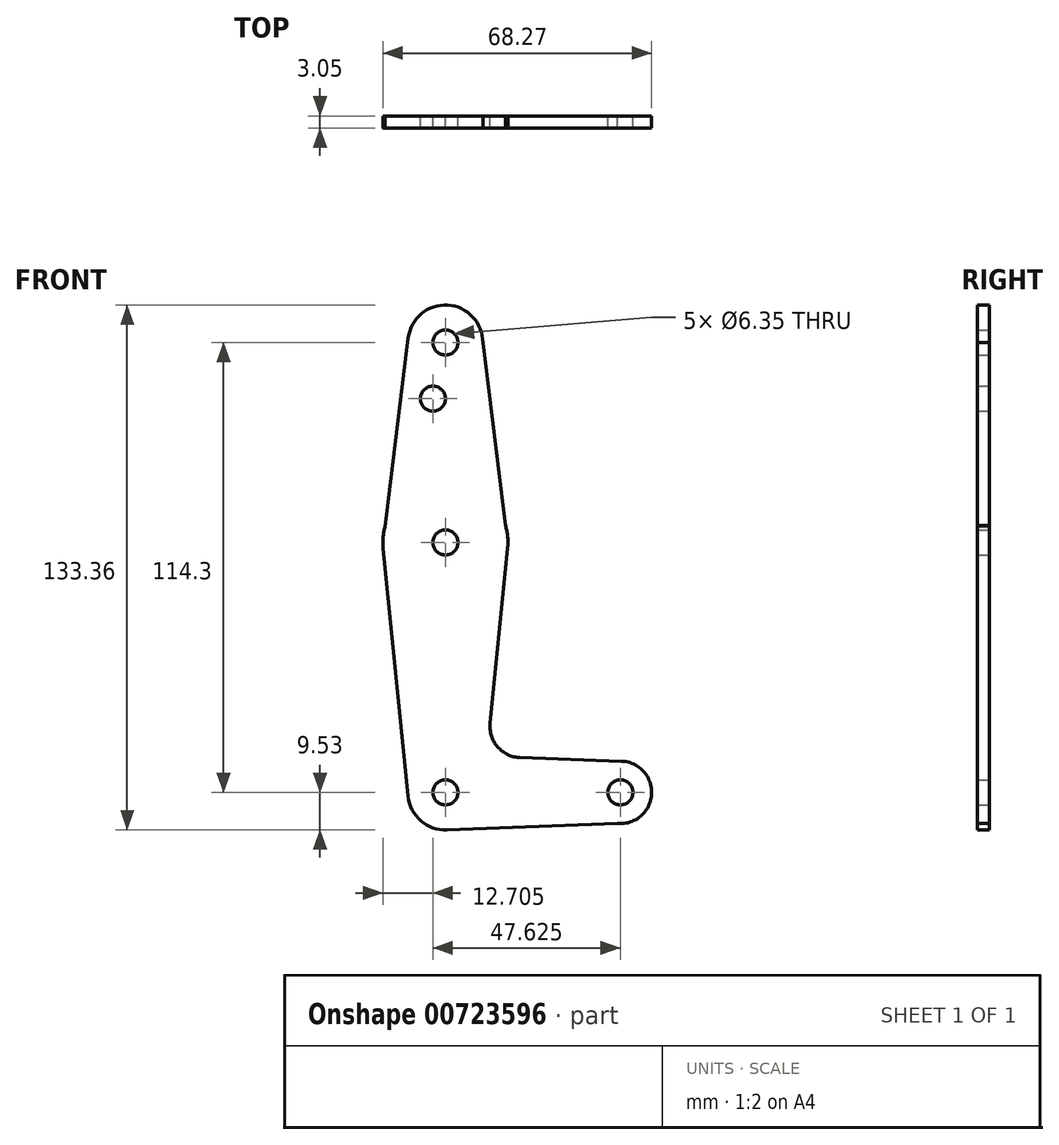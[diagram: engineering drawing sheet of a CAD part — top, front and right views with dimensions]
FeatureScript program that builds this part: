
annotation { "Feature Type Name" : "Feature", "Feature Type Description" : "" }
export const myFeature = defineFeature(function(context is Context, id is Id, definition is map)
    precondition{}
    {
        {
            var Q0;
            Q0=qCreatedBy(makeId("Front.planeOp"),FACE);
            var sketch = newSketch(context, id + "F0", { "sketchPlane" : qUnion([Q0])});
            skLineSegment(sketch, "E0", {"start": v(0, 114.3) * mm, "end": v(0, 0) * mm, "construction": true});
            skLineSegment(sketch, "E1", {"start": v(0, 0) * mm, "end": v(44.45, 0) * mm, "construction": true});
            skCircle(sketch, "E2", {"center": v(0, 114.3) * mm, "radius": 9.53 * mm});
            skCircle(sketch, "E3", {"center": v(0, 0) * mm, "radius": 9.53 * mm});
            skCircle(sketch, "E4", {"center": v(44.45, 0) * mm, "radius": 7.94 * mm});
            skCircle(sketch, "E5", {"center": v(0, 63.5) * mm, "radius": 15.88 * mm});
            skLineSegment(sketch, "E6", {"start": v(18.97, 8.85) * mm, "end": v(44.73, 7.93) * mm});
            skLineSegment(sketch, "E7", {"start": v(43.71, -7.9) * mm, "end": v(0.35, -9.52) * mm});
            skLineSegment(sketch, "E8", {"start": v(-9.45, 115.47) * mm, "end": v(-15.4, 67.39) * mm});
            skLineSegment(sketch, "E9", {"start": v(-15.8, 61.91) * mm, "end": v(-9.48, -0.95) * mm});
            skLineSegment(sketch, "E10", {"start": v(9.52, 114.3) * mm, "end": v(15.27, 67.86) * mm});
            skLineSegment(sketch, "E11", {"start": v(15.8, 61.91) * mm, "end": v(11.34, 17.59) * mm});
            skCircle(sketch, "E12", {"center": v(0, 114.3) * mm, "radius": 3.18 * mm});
            skCircle(sketch, "E13", {"center": v(-3.17, 100.03) * mm, "radius": 3.18 * mm});
            skCircle(sketch, "E14", {"center": v(0, 63.5) * mm, "radius": 3.18 * mm});
            skCircle(sketch, "E15", {"center": v(0, 0) * mm, "radius": 3.18 * mm});
            skArc(sketch, "E16.filletArc", {"start": v(11.34, 17.59) * mm, "mid": v(13.26, 11.57) * mm, "end": v(18.97, 8.85) * mm});
            skCircle(sketch, "E17", {"center": v(44.45, 0) * mm, "radius": 3.18 * mm});
            skSolve(sketch);
        }
        {
            var Q0;
            Q0 = qSketchRegion(id + "F0", true);
            extrude(context, id + "F1", {"entities" : qUnion([Q0]), "depth" : 3.05 * mm, "offsetDistance" : 25.4 * mm});
        }
    });
